# Revit family: Beer Cooler- 4 coils-110 LTR-HR Assembly Line C-2048
name_source: partatom
category: Furniture
revit_build: Autodesk Revit 2018 (Build: 20181015_0930(x64)
units: mm (PartAtom-declared; Revit-internal decimal feet)

## family parameters
Always vertical = Yes
Cut with Voids When Loaded = No
OmniClass Number = 23.40.20.00
OmniClass Title = General Furniture and Specialties
Room Calculation Point = No
Shared = No
Work Plane-Based = No

## types (1)
- Beer Cooler- 4 coils-110 LTR/HR Assembly Line C2048
    Model = C 2048
    URL = https://kromedispense.co.in
    eli = 200 mm  [stored 0.656168 ft]
    height = 560 mm  [stored 1.83727 ft]
    hh = 542 mm
    length = 616 mm  [stored 2.021 ft]
    r = 80 mm  [stored 0.262467 ft]
    thin = 8 mm  [stored 0.0262467 ft]
    width = 455 mm

note: [stored X ft] marks values corroborated as IEEE doubles in the binary element streams (Revit-internal decimal feet)

## geometry (parser evidence)
native form markers: Sweep x3
no freeform markers — native parametric forms only
